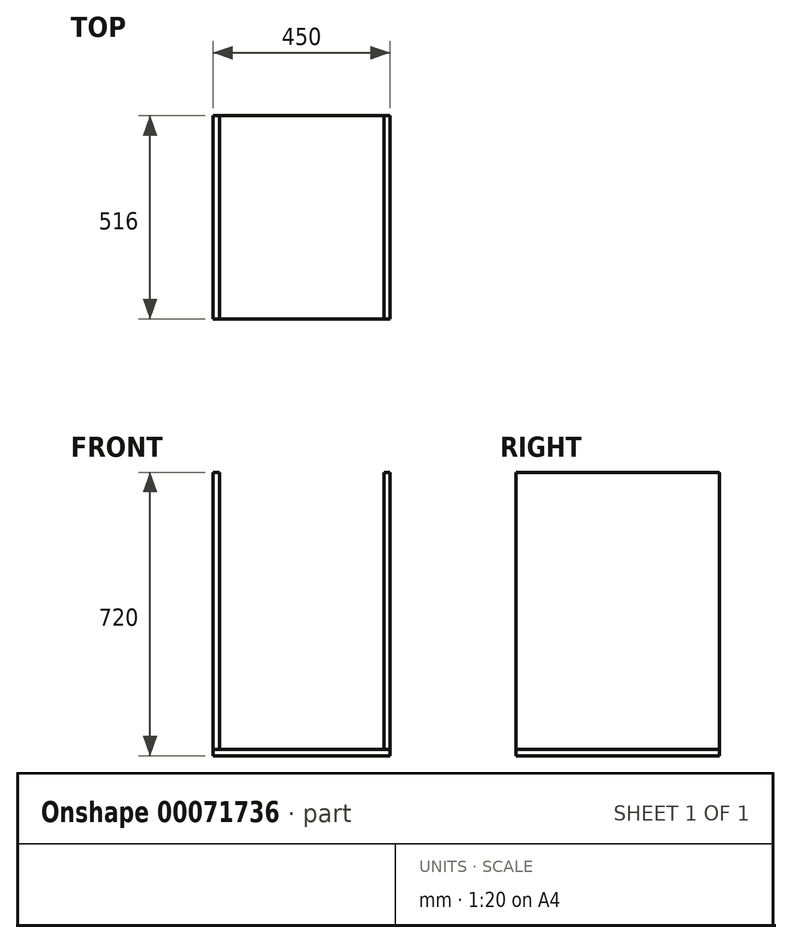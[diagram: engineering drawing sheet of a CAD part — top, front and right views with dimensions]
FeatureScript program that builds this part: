
annotation { "Feature Type Name" : "Feature", "Feature Type Description" : "" }
export const myFeature = defineFeature(function(context is Context, id is Id, definition is map)
    precondition{}
    {
        {
            var Q0;
            Q0=qCreatedBy(makeId("Right.planeOp"),FACE);
            var sketch = newSketch(context, id + "F0", { "sketchPlane" : qUnion([Q0])});
            skLineSegment(sketch, "E0.bottom", {"start": v(0, 0) * mm, "end": v(516, 0) * mm});
            skLineSegment(sketch, "E0.top", {"start": v(0, 704) * mm, "end": v(516, 704) * mm});
            skLineSegment(sketch, "E0.left", {"start": v(0, 0) * mm, "end": v(0, 704) * mm});
            skLineSegment(sketch, "E0.right", {"start": v(516, 0) * mm, "end": v(516, 704) * mm});
            skSolve(sketch);
        }
        {
            var Q0;
            Q0 = qSketchRegion(id + "F0", true);
            extrude(context, id + "F1", {"entities" : qUnion([Q0]), "depth" : 16 * mm});
        }
        {
            var Q0;
            Q0=qCreatedBy(makeId("Top.planeOp"),FACE);
            var sketch = newSketch(context, id + "F2", { "sketchPlane" : qUnion([Q0])});
            skLineSegment(sketch, "E1.bottom", {"start": v(0, 0) * mm, "end": v(450, 0) * mm});
            skLineSegment(sketch, "E1.top", {"start": v(0, 516) * mm, "end": v(450, 516) * mm});
            skLineSegment(sketch, "E1.left", {"start": v(0, 0) * mm, "end": v(0, 516) * mm});
            skLineSegment(sketch, "E1.right", {"start": v(450, 0) * mm, "end": v(450, 516) * mm});
            skSolve(sketch);
        }
        {
            var Q0;
            Q0=makeQuery(id+"F2.imprint","IMPRINT",FACE,{"disambiguationData":[TD([[makeQuery(id+"F2.imprint","IMPRINT",EDGE,{"derivedFrom":sQuery(id+"F2.wireOp",EDGE,"E1.bottom")}),1.0]])]});
            extrude(context, id + "F3", {"entities" : qUnion([Q0]), "oppositeDirection" : true, "depth" : 16 * mm});
        }
        {
            var Q0;
            Q0=makeQuery(id+"F3.opExtrude","SWEPT_FACE",FACE,{"disambiguationData":[OSD([sQuery(id+"F2.wireOp",EDGE,"E1.right")])]});
            var sketch = newSketch(context, id + "F4", { "sketchPlane" : qUnion([Q0])});
            skLineSegment(sketch, "E2.bottom", {"start": v(0, 0) * mm, "end": v(516, 0) * mm});
            skLineSegment(sketch, "E2.top", {"start": v(0, 704) * mm, "end": v(516, 704) * mm});
            skLineSegment(sketch, "E2.left", {"start": v(0, 0) * mm, "end": v(0, 704) * mm});
            skLineSegment(sketch, "E2.right", {"start": v(516, 0) * mm, "end": v(516, 704) * mm});
            skSolve(sketch);
        }
        {
            var Q0;
            Q0=makeQuery(id+"F4.imprint","IMPRINT",FACE,{"disambiguationData":[TD([[makeQuery(id+"F4.imprint","IMPRINT",EDGE,{"derivedFrom":sQuery(id+"F4.wireOp",EDGE,"E2.top")}),-1.0]])]});
            extrude(context, id + "F5", {"entities" : qUnion([Q0]), "oppositeDirection" : true, "depth" : 16 * mm});
        }
    });
